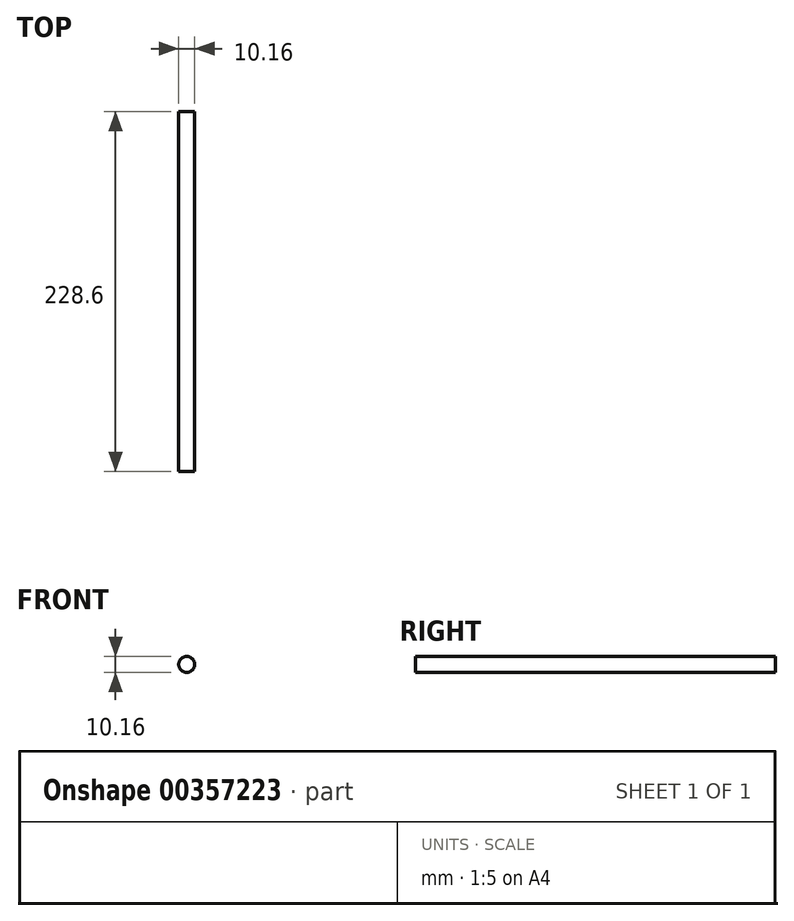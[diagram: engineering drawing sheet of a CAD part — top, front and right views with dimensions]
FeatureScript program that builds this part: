
annotation { "Feature Type Name" : "Feature", "Feature Type Description" : "" }
export const myFeature = defineFeature(function(context is Context, id is Id, definition is map)
    precondition{}
    {
        {
            var Q0;
            Q0=qCreatedBy(makeId("Front.planeOp"),FACE);
            var sketch = newSketch(context, id + "F0", { "sketchPlane" : qUnion([Q0])});
            skCircle(sketch, "E0", {"center": v(-1.1, 1.85) * mm, "radius": 5.08 * mm});
            skSolve(sketch);
        }
        {
            var Q0;
            Q0=makeQuery(id+"F0.imprint","IMPRINT",FACE,{"disambiguationData":[TD([[makeQuery(id+"F0.imprint","IMPRINT",EDGE,{"derivedFrom":sQuery(id+"F0.wireOp",EDGE,"E0")}),1.0]])]});
            extrude(context, id + "F1", {"entities" : qUnion([Q0]), "depth" : 228.6 * mm});
        }
    });
